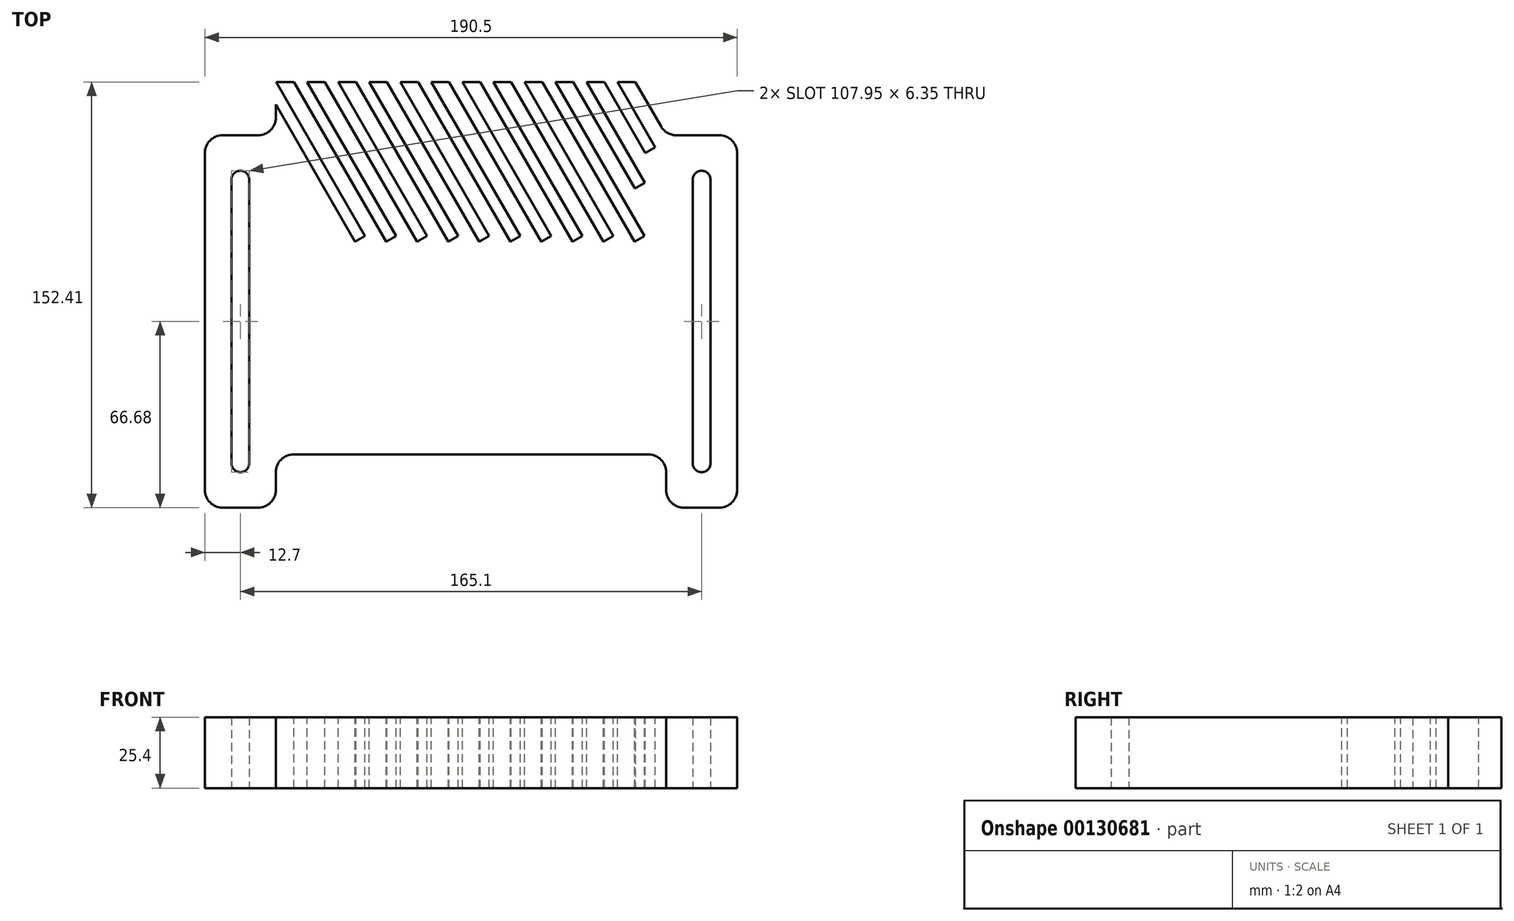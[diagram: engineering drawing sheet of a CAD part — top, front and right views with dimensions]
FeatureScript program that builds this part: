
annotation { "Feature Type Name" : "Feature", "Feature Type Description" : "" }
export const myFeature = defineFeature(function(context is Context, id is Id, definition is map)
    precondition{}
    {
        {
            var Q0;
            Q0=qCreatedBy(makeId("Top.planeOp"),FACE);
            var sketch = newSketch(context, id + "F0", { "sketchPlane" : qUnion([Q0])});
            skLineSegment(sketch, "E0.bottom", {"start": v(0, 66.68) * mm, "end": v(-69.85, 66.68) * mm});
            skLineSegment(sketch, "E0.top", {"start": v(0, -66.68) * mm, "end": v(-63.5, -66.67) * mm});
            skLineSegment(sketch, "E0.left", {"start": v(0, 66.68) * mm, "end": v(0, -66.68) * mm, "construction": true});
            skLineSegment(sketch, "E0.right", {"start": v(-69.85, 66.68) * mm, "end": v(-69.85, 53.98) * mm});
            skLineSegment(sketch, "E1.bottom", {"start": v(-88.9, 47.63) * mm, "end": v(-76.2, 47.63) * mm});
            skLineSegment(sketch, "E1.top", {"start": v(-88.9, -85.72) * mm, "end": v(-76.2, -85.72) * mm});
            skLineSegment(sketch, "E1.left", {"start": v(-95.25, 41.28) * mm, "end": v(-95.25, -79.37) * mm});
            skLineSegment(sketch, "E1.right", {"start": v(-69.85, -73.02) * mm, "end": v(-69.85, -79.37) * mm});
            skArc(sketch, "E2", {"start": v(-79.37, 31.75) * mm, "mid": v(-82.55, 34.93) * mm, "end": v(-85.72, 31.75) * mm});
            skArc(sketch, "E3", {"start": v(-85.73, -69.85) * mm, "mid": v(-82.55, -73.02) * mm, "end": v(-79.38, -69.85) * mm});
            skLineSegment(sketch, "E4", {"start": v(-85.72, 31.75) * mm, "end": v(-85.73, -69.85) * mm});
            skLineSegment(sketch, "E5", {"start": v(-79.37, 31.75) * mm, "end": v(-79.38, -69.85) * mm});
            skPoint(sketch, "E6.visualSharp", {"position": v(-95.25, 47.63) * mm});
            skArc(sketch, "E6.filletArc", {"start": v(-88.9, 47.63) * mm, "mid": v(-93.4, 45.77) * mm, "end": v(-95.25, 41.28) * mm});
            skPoint(sketch, "E7.visualSharp", {"position": v(-95.25, -85.72) * mm});
            skArc(sketch, "E7.filletArc", {"start": v(-95.25, -79.37) * mm, "mid": v(-93.4, -83.87) * mm, "end": v(-88.9, -85.72) * mm});
            skPoint(sketch, "E8.visualSharp", {"position": v(-69.85, -85.72) * mm});
            skArc(sketch, "E8.filletArc", {"start": v(-76.2, -85.72) * mm, "mid": v(-71.7, -83.87) * mm, "end": v(-69.85, -79.37) * mm});
            skPoint(sketch, "E9.visualSharp", {"position": v(-69.85, -66.68) * mm});
            skArc(sketch, "E9.filletArc", {"start": v(-63.5, -66.67) * mm, "mid": v(-68, -68.53) * mm, "end": v(-69.85, -73.02) * mm});
            skArc(sketch, "E10.MirrorCS", {"start": v(76.2, -85.72) * mm, "mid": v(71.7, -83.87) * mm, "end": v(69.85, -79.37) * mm});
            skArc(sketch, "E11.MirrorCS", {"start": v(95.25, -79.37) * mm, "mid": v(93.4, -83.87) * mm, "end": v(88.9, -85.72) * mm});
            skArc(sketch, "E12.MirrorCS", {"start": v(63.5, -66.67) * mm, "mid": v(68, -68.53) * mm, "end": v(69.85, -73.02) * mm});
            skArc(sketch, "E13.MirrorCS", {"start": v(88.9, 47.63) * mm, "mid": v(93.4, 45.77) * mm, "end": v(95.25, 41.28) * mm});
            skLineSegment(sketch, "E14.MirrorCS", {"start": v(79.38, 31.75) * mm, "end": v(79.38, -69.85) * mm});
            skLineSegment(sketch, "E15.MirrorCS", {"start": v(85.72, 31.75) * mm, "end": v(85.72, -69.85) * mm});
            skPoint(sketch, "E16.MirrorP", {"position": v(69.85, -85.72) * mm});
            skLineSegment(sketch, "E17.MirrorCS", {"start": v(95.25, 41.28) * mm, "end": v(95.25, -79.37) * mm});
            skLineSegment(sketch, "E18.MirrorCS", {"start": v(88.9, -85.73) * mm, "end": v(76.2, -85.73) * mm});
            skLineSegment(sketch, "E19.MirrorCS", {"start": v(0, -66.68) * mm, "end": v(63.5, -66.68) * mm});
            skPoint(sketch, "E20.MirrorP", {"position": v(69.85, -66.68) * mm});
            skLineSegment(sketch, "E21.MirrorCS", {"start": v(0, 66.68) * mm, "end": v(58.85, 66.68) * mm});
            skPoint(sketch, "E22.MirrorP", {"position": v(95.25, 47.63) * mm});
            skPoint(sketch, "E23.MirrorP", {"position": v(95.25, -85.72) * mm});
            skLineSegment(sketch, "E24.MirrorCS", {"start": v(88.9, 47.62) * mm, "end": v(73.52, 47.62) * mm});
            skArc(sketch, "E25.MirrorCS", {"start": v(79.37, 31.75) * mm, "mid": v(82.55, 34.93) * mm, "end": v(85.72, 31.75) * mm});
            skArc(sketch, "E26.MirrorCS", {"start": v(85.73, -69.85) * mm, "mid": v(82.55, -73.02) * mm, "end": v(79.38, -69.85) * mm});
            skLineSegment(sketch, "E27.MirrorCS", {"start": v(69.85, -73.02) * mm, "end": v(69.85, -79.37) * mm});
            skPoint(sketch, "E28", {"position": v(0, 0) * mm});
            skLineSegment(sketch, "E29", {"start": v(68.02, 50.8) * mm, "end": v(58.85, 66.68) * mm});
            skPoint(sketch, "E30.visualSharp", {"position": v(-69.85, 47.63) * mm});
            skArc(sketch, "E30.filletArc", {"start": v(-76.2, 47.63) * mm, "mid": v(-71.7, 49.48) * mm, "end": v(-69.85, 53.98) * mm});
            skPoint(sketch, "E31.visualSharp", {"position": v(69.85, 47.63) * mm});
            skArc(sketch, "E31.filletArc", {"start": v(68.02, 50.8) * mm, "mid": v(70.34, 48.48) * mm, "end": v(73.52, 47.63) * mm});
            skSolve(sketch);
        }
        {
            var Q0;
            Q0=makeQuery(id+"F0.imprint","IMPRINT",FACE,{"disambiguationData":[TD([[makeQuery(id+"F0.imprint","IMPRINT",EDGE,{"derivedFrom":sQuery(id+"F0.wireOp",EDGE,"E0.bottom")}),1.0]])]});
            extrude(context, id + "F1", {"entities" : qUnion([Q0]), "depth" : 25.4 * mm});
        }
        {
            var Q0;
            Q0=makeQuery(id+"F1.opExtrude","CAP_FACE",FACE,{"disambiguationData":[OSD([sQuery(id+"F0.wireOp",EDGE,"E0.bottom"),sQuery(id+"F0.wireOp",EDGE,"E0.top"),sQuery(id+"F0.wireOp",EDGE,"E0.right"),sQuery(id+"F0.wireOp",EDGE,"E1.bottom"),sQuery(id+"F0.wireOp",EDGE,"E1.top"),sQuery(id+"F0.wireOp",EDGE,"E1.left"),sQuery(id+"F0.wireOp",EDGE,"E1.right"),sQuery(id+"F0.wireOp",EDGE,"E2"),sQuery(id+"F0.wireOp",EDGE,"E3"),sQuery(id+"F0.wireOp",EDGE,"E4"),sQuery(id+"F0.wireOp",EDGE,"E5"),sQuery(id+"F0.wireOp",EDGE,"E6.filletArc"),sQuery(id+"F0.wireOp",EDGE,"E7.filletArc"),sQuery(id+"F0.wireOp",EDGE,"E8.filletArc"),sQuery(id+"F0.wireOp",EDGE,"E9.filletArc"),sQuery(id+"F0.wireOp",EDGE,"E10.MirrorCS"),sQuery(id+"F0.wireOp",EDGE,"E11.MirrorCS"),sQuery(id+"F0.wireOp",EDGE,"E12.MirrorCS"),sQuery(id+"F0.wireOp",EDGE,"E13.MirrorCS"),sQuery(id+"F0.wireOp",EDGE,"E14.MirrorCS"),sQuery(id+"F0.wireOp",EDGE,"E15.MirrorCS"),sQuery(id+"F0.wireOp",EDGE,"E17.MirrorCS"),sQuery(id+"F0.wireOp",EDGE,"E18.MirrorCS"),sQuery(id+"F0.wireOp",EDGE,"E19.MirrorCS"),sQuery(id+"F0.wireOp",EDGE,"E21.MirrorCS"),sQuery(id+"F0.wireOp",EDGE,"E24.MirrorCS"),sQuery(id+"F0.wireOp",EDGE,"E25.MirrorCS"),sQuery(id+"F0.wireOp",EDGE,"E26.MirrorCS"),sQuery(id+"F0.wireOp",EDGE,"E27.MirrorCS"),sQuery(id+"F0.wireOp",EDGE,"E29"),sQuery(id+"F0.wireOp",EDGE,"E30.filletArc"),sQuery(id+"F0.wireOp",EDGE,"E31.filletArc")])],"isStart":false});
            var sketch = newSketch(context, id + "F2", { "sketchPlane" : qUnion([Q0])});
            skLineSegment(sketch, "E32", {"start": v(52.5, 66.68) * mm, "end": v(65.98, 43.34) * mm});
            skLineSegment(sketch, "E33", {"start": v(65.98, 43.34) * mm, "end": v(62.4, 41.28) * mm});
            skLineSegment(sketch, "E34", {"start": v(62.4, 41.28) * mm, "end": v(47.74, 66.68) * mm});
            skLineSegment(sketch, "E35", {"start": v(47.74, 66.68) * mm, "end": v(52.5, 66.68) * mm});
            skSolve(sketch);
        }
        {
            var Q0;
            Q0 = qSketchRegion(id + "F2", true);
            extrude(context, id + "F3", {"entities" : qUnion([Q0]), "operationType" : NewBodyOperationType.REMOVE, "endBound" : BoundingType.THROUGH_ALL, "oppositeDirection" : true, "depth" : 25.4 * mm});
        }
        {
            var Q0;
            Q0=makeQuery(id+"F1.opExtrude","CAP_FACE",FACE,{"disambiguationData":[OSD([sQuery(id+"F0.wireOp",EDGE,"E0.bottom"),sQuery(id+"F0.wireOp",EDGE,"E0.top"),sQuery(id+"F0.wireOp",EDGE,"E0.right"),sQuery(id+"F0.wireOp",EDGE,"E1.bottom"),sQuery(id+"F0.wireOp",EDGE,"E1.top"),sQuery(id+"F0.wireOp",EDGE,"E1.left"),sQuery(id+"F0.wireOp",EDGE,"E1.right"),sQuery(id+"F0.wireOp",EDGE,"E2"),sQuery(id+"F0.wireOp",EDGE,"E3"),sQuery(id+"F0.wireOp",EDGE,"E4"),sQuery(id+"F0.wireOp",EDGE,"E5"),sQuery(id+"F0.wireOp",EDGE,"E6.filletArc"),sQuery(id+"F0.wireOp",EDGE,"E7.filletArc"),sQuery(id+"F0.wireOp",EDGE,"E8.filletArc"),sQuery(id+"F0.wireOp",EDGE,"E9.filletArc"),sQuery(id+"F0.wireOp",EDGE,"E10.MirrorCS"),sQuery(id+"F0.wireOp",EDGE,"E11.MirrorCS"),sQuery(id+"F0.wireOp",EDGE,"E12.MirrorCS"),sQuery(id+"F0.wireOp",EDGE,"E13.MirrorCS"),sQuery(id+"F0.wireOp",EDGE,"E14.MirrorCS"),sQuery(id+"F0.wireOp",EDGE,"E15.MirrorCS"),sQuery(id+"F0.wireOp",EDGE,"E17.MirrorCS"),sQuery(id+"F0.wireOp",EDGE,"E18.MirrorCS"),sQuery(id+"F0.wireOp",EDGE,"E19.MirrorCS"),sQuery(id+"F0.wireOp",EDGE,"E21.MirrorCS"),sQuery(id+"F0.wireOp",EDGE,"E24.MirrorCS"),sQuery(id+"F0.wireOp",EDGE,"E25.MirrorCS"),sQuery(id+"F0.wireOp",EDGE,"E26.MirrorCS"),sQuery(id+"F0.wireOp",EDGE,"E27.MirrorCS"),sQuery(id+"F0.wireOp",EDGE,"E29"),sQuery(id+"F0.wireOp",EDGE,"E30.filletArc"),sQuery(id+"F0.wireOp",EDGE,"E31.filletArc")])],"isStart":false});
            var sketch = newSketch(context, id + "F4", { "sketchPlane" : qUnion([Q0])});
            skLineSegment(sketch, "E36", {"start": v(41.39, 66.68) * mm, "end": v(62.2, 30.64) * mm});
            skLineSegment(sketch, "E37", {"start": v(62.2, 30.64) * mm, "end": v(58.62, 28.58) * mm});
            skLineSegment(sketch, "E38", {"start": v(58.62, 28.58) * mm, "end": v(36.63, 66.68) * mm});
            skLineSegment(sketch, "E39", {"start": v(36.63, 66.68) * mm, "end": v(41.39, 66.68) * mm});
            skLineSegment(sketch, "E40", {"start": v(30.28, 66.68) * mm, "end": v(62.08, 11.59) * mm});
            skLineSegment(sketch, "E41", {"start": v(62.08, 11.59) * mm, "end": v(58.5, 9.53) * mm});
            skLineSegment(sketch, "E42", {"start": v(58.5, 9.53) * mm, "end": v(25.51, 66.68) * mm});
            skLineSegment(sketch, "E43", {"start": v(25.51, 66.68) * mm, "end": v(30.28, 66.68) * mm});
            skLineSegment(sketch, "E44.1.0.0", {"start": v(14.4, 66.68) * mm, "end": v(19.16, 66.68) * mm});
            skLineSegment(sketch, "E44.1.0.1", {"start": v(19.16, 66.68) * mm, "end": v(50.97, 11.59) * mm});
            skLineSegment(sketch, "E44.1.0.2", {"start": v(47.4, 9.53) * mm, "end": v(14.4, 66.68) * mm});
            skLineSegment(sketch, "E44.1.0.3", {"start": v(50.97, 11.59) * mm, "end": v(47.4, 9.53) * mm});
            skLineSegment(sketch, "E44.2.0.0", {"start": v(3.29, 66.68) * mm, "end": v(8.05, 66.68) * mm});
            skLineSegment(sketch, "E44.2.0.1", {"start": v(8.05, 66.68) * mm, "end": v(39.86, 11.59) * mm});
            skLineSegment(sketch, "E44.2.0.2", {"start": v(36.28, 9.53) * mm, "end": v(3.29, 66.68) * mm});
            skLineSegment(sketch, "E44.2.0.3", {"start": v(39.86, 11.59) * mm, "end": v(36.28, 9.53) * mm});
            skLineSegment(sketch, "E44.3.0.0", {"start": v(-7.82, 66.68) * mm, "end": v(-3.06, 66.68) * mm});
            skLineSegment(sketch, "E44.3.0.1", {"start": v(-3.06, 66.68) * mm, "end": v(28.74, 11.59) * mm});
            skLineSegment(sketch, "E44.3.0.2", {"start": v(25.17, 9.53) * mm, "end": v(-7.82, 66.68) * mm});
            skLineSegment(sketch, "E44.3.0.3", {"start": v(28.74, 11.59) * mm, "end": v(25.17, 9.53) * mm});
            skLineSegment(sketch, "E44.4.0.0", {"start": v(-18.94, 66.68) * mm, "end": v(-14.17, 66.68) * mm});
            skLineSegment(sketch, "E44.4.0.1", {"start": v(-14.17, 66.68) * mm, "end": v(17.63, 11.59) * mm});
            skLineSegment(sketch, "E44.4.0.2", {"start": v(14.06, 9.53) * mm, "end": v(-18.94, 66.68) * mm});
            skLineSegment(sketch, "E44.4.0.3", {"start": v(17.63, 11.59) * mm, "end": v(14.06, 9.53) * mm});
            skLineSegment(sketch, "E44.5.0.0", {"start": v(-30.05, 66.68) * mm, "end": v(-25.29, 66.68) * mm});
            skLineSegment(sketch, "E44.5.0.1", {"start": v(-25.29, 66.68) * mm, "end": v(6.52, 11.59) * mm});
            skLineSegment(sketch, "E44.5.0.2", {"start": v(2.95, 9.53) * mm, "end": v(-30.05, 66.68) * mm});
            skLineSegment(sketch, "E44.5.0.3", {"start": v(6.52, 11.59) * mm, "end": v(2.95, 9.53) * mm});
            skLineSegment(sketch, "E44.6.0.0", {"start": v(-41.16, 66.68) * mm, "end": v(-36.4, 66.68) * mm});
            skLineSegment(sketch, "E44.6.0.1", {"start": v(-36.4, 66.68) * mm, "end": v(-4.6, 11.59) * mm});
            skLineSegment(sketch, "E44.6.0.2", {"start": v(-8.17, 9.53) * mm, "end": v(-41.16, 66.68) * mm});
            skLineSegment(sketch, "E44.6.0.3", {"start": v(-4.6, 11.59) * mm, "end": v(-8.17, 9.53) * mm});
            skLineSegment(sketch, "E44.7.0.0", {"start": v(-52.27, 66.68) * mm, "end": v(-47.51, 66.68) * mm});
            skLineSegment(sketch, "E44.7.0.1", {"start": v(-47.51, 66.68) * mm, "end": v(-15.7, 11.59) * mm});
            skLineSegment(sketch, "E44.7.0.2", {"start": v(-19.28, 9.53) * mm, "end": v(-52.27, 66.68) * mm});
            skLineSegment(sketch, "E44.7.0.3", {"start": v(-15.7, 11.59) * mm, "end": v(-19.28, 9.53) * mm});
            skLineSegment(sketch, "E44.8.0.0", {"start": v(-63.39, 66.68) * mm, "end": v(-58.62, 66.68) * mm});
            skLineSegment(sketch, "E44.8.0.1", {"start": v(-58.62, 66.68) * mm, "end": v(-26.82, 11.59) * mm});
            skLineSegment(sketch, "E44.8.0.2", {"start": v(-30.4, 9.53) * mm, "end": v(-63.39, 66.68) * mm});
            skLineSegment(sketch, "E44.8.0.3", {"start": v(-26.82, 11.59) * mm, "end": v(-30.4, 9.53) * mm});
            skLineSegment(sketch, "E44.9.0.0", {"start": v(-74.5, 66.68) * mm, "end": v(-69.74, 66.68) * mm});
            skLineSegment(sketch, "E44.9.0.1", {"start": v(-69.74, 66.68) * mm, "end": v(-37.93, 11.59) * mm});
            skLineSegment(sketch, "E44.9.0.2", {"start": v(-41.5, 9.53) * mm, "end": v(-74.5, 66.68) * mm});
            skLineSegment(sketch, "E44.9.0.3", {"start": v(-37.93, 11.59) * mm, "end": v(-41.5, 9.53) * mm});
            skLineSegment(sketch, "E44.direction1", {"start": v(25.51, 66.68) * mm, "end": v(14.4, 66.68) * mm, "construction": true});
            skSolve(sketch);
        }
        {
            var Q0;
            Q0 = qSketchRegion(id + "F4", true);
            extrude(context, id + "F5", {"entities" : qUnion([Q0]), "operationType" : NewBodyOperationType.REMOVE, "endBound" : BoundingType.THROUGH_ALL, "oppositeDirection" : true, "depth" : 25.4 * mm});
        }
    });
